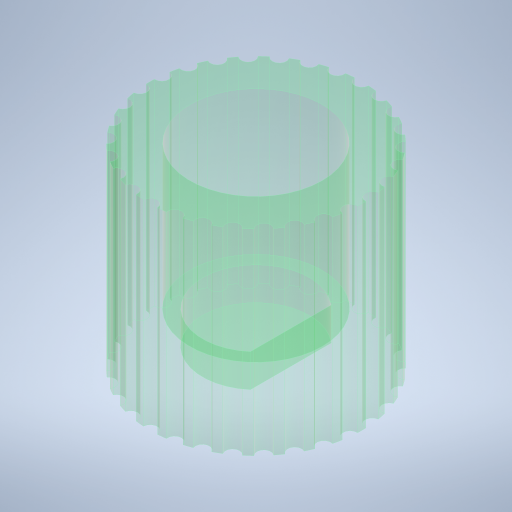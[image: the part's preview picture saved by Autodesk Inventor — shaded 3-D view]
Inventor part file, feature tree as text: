
AUTODESK INVENTOR PART (.ipt)
format: ipt  version: 2024 (Build 280153000, 153)  size: 370,176 bytes
history: native  units: mm
features: extrude x4, sketch x4, pattern_circular x1
ambient origin geometry x8: Origin, YZ Plane, XZ Plane, XY Plane, X Axis, Y Axis, Z Axis, Center Point
bodies: Solid1 (feature_tree)
feature tree (9):
  extrude  "Extrusion1"  Depth=3.0mm TaperAngle=0.0deg
  extrude  "Extrusion2"  Depth=5.0mm
  extrude  "Extrusion4"  Depth=8.14mm TaperAngle=0.0deg
  extrude  "Extrusion5"  Depth=10.0mm
  pattern_circular  "Circular Pattern2"  [2 undecoded]
  sketch  "Sketch1"  dims[d0=12.0mm d1=3.0mm d2=0.0mm]
  sketch  "Sketch2"  dims[d3=6.05mm d4=5.0mm]
  sketch  "Sketch4"  dims[d5=1.86mm d6=0.0mm d13=8.14mm d14=0.0mm]
  sketch  "Sketch5"  dims[d15=7.5mm d16=12.0mm d17=0.8mm d18=10.0mm d19=0.0mm d20=300.0mm d21=360.0deg d23=0.5mm d24=0.872665mm d25=0.5mm d26=0.872665mm]
note: 2 required parameter values undecoded (feature->parameter linkage not recoverable at this tier; creation-order binding heuristic only, values carry confidence <= 0.55)
